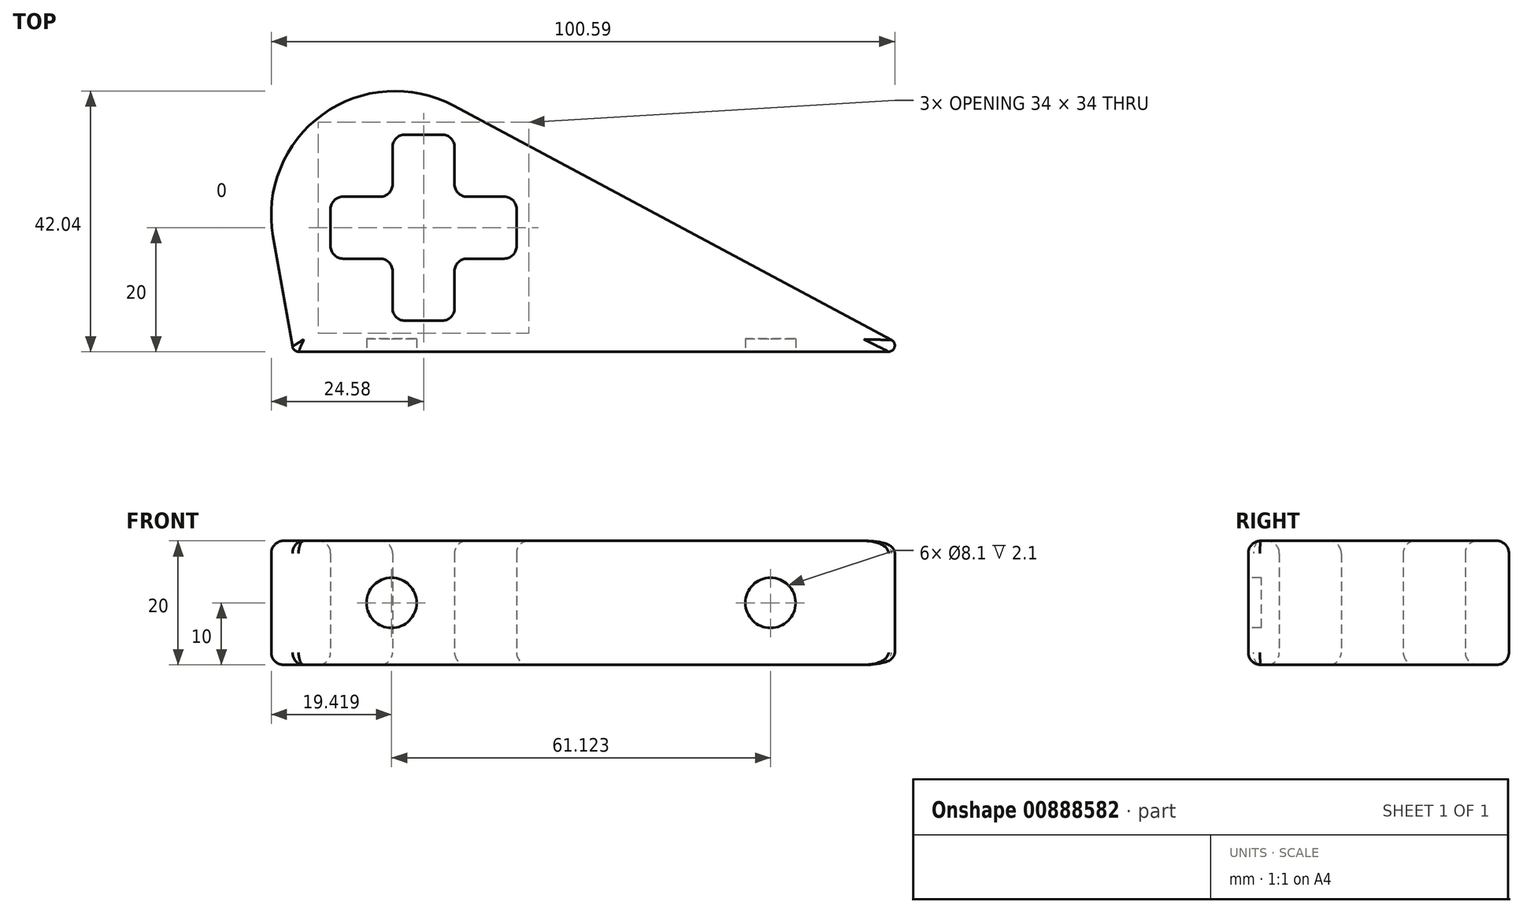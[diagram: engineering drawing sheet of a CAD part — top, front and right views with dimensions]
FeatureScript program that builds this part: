
annotation { "Feature Type Name" : "Feature", "Feature Type Description" : "" }
export const myFeature = defineFeature(function(context is Context, id is Id, definition is map)
    precondition{}
    {
        {
            var Q0;
            Q0=qCreatedBy(makeId("Top.planeOp"),FACE);
            var sketch = newSketch(context, id + "F0", { "sketchPlane" : qUnion([Q0])});
            skLineSegment(sketch, "E0.bottom", {"start": v(-13, -5) * mm, "end": v(-7, -5) * mm});
            skLineSegment(sketch, "E0.top", {"start": v(-13, 5) * mm, "end": v(-7, 5) * mm});
            skLineSegment(sketch, "E0.left", {"start": v(-15, -3) * mm, "end": v(-15, 3) * mm});
            skLineSegment(sketch, "E0.right", {"start": v(15, -3) * mm, "end": v(15, 3) * mm});
            skPoint(sketch, "E0.middle", {"position": v(0, 0) * mm});
            skPoint(sketch, "E1.visualSharp", {"position": v(-15, 5) * mm});
            skArc(sketch, "E1.filletArc", {"start": v(-13, 5) * mm, "mid": v(-14.41, 4.41) * mm, "end": v(-15, 3) * mm});
            skPoint(sketch, "E2.visualSharp", {"position": v(15, 5) * mm});
            skArc(sketch, "E2.filletArc", {"start": v(15, 3) * mm, "mid": v(14.41, 4.41) * mm, "end": v(13, 5) * mm});
            skPoint(sketch, "E3.visualSharp", {"position": v(15, -5) * mm});
            skArc(sketch, "E3.filletArc", {"start": v(13, -5) * mm, "mid": v(14.41, -4.41) * mm, "end": v(15, -3) * mm});
            skPoint(sketch, "E4.visualSharp", {"position": v(-15, -5) * mm});
            skArc(sketch, "E4.filletArc", {"start": v(-15, -3) * mm, "mid": v(-14.41, -4.41) * mm, "end": v(-13, -5) * mm});
            skLineSegment(sketch, "E5", {"start": v(-20.16, -20) * mm, "end": v(75.01, -20) * mm});
            skLineSegment(sketch, "E6", {"start": v(75.48, -18.12) * mm, "end": v(4.86, 19.68) * mm});
            skLineSegment(sketch, "E7", {"start": v(-24.27, -1.43) * mm, "end": v(-21.15, -19.17) * mm});
            skPoint(sketch, "E8.visualSharp", {"position": v(-31.42, 39.09) * mm});
            skArc(sketch, "E8.filletArc", {"start": v(4.86, 19.68) * mm, "mid": v(-16.31, 18.24) * mm, "end": v(-24.27, -1.43) * mm});
            skPoint(sketch, "E9.visualSharp", {"position": v(79, -20) * mm});
            skArc(sketch, "E9.filletArc", {"start": v(75.01, -20) * mm, "mid": v(75.98, -19.24) * mm, "end": v(75.48, -18.12) * mm});
            skPoint(sketch, "E10.visualSharp", {"position": v(-21, -20) * mm});
            skArc(sketch, "E10.filletArc", {"start": v(-21.15, -19.17) * mm, "mid": v(-20.8, -19.77) * mm, "end": v(-20.16, -20) * mm});
            skLineSegment(sketch, "E11.bottom", {"start": v(-3, -15) * mm, "end": v(3, -15) * mm});
            skLineSegment(sketch, "E11.top", {"start": v(-3, 15) * mm, "end": v(3, 15) * mm});
            skLineSegment(sketch, "E11.left", {"start": v(-5, -13) * mm, "end": v(-5, -7) * mm});
            skLineSegment(sketch, "E11.right", {"start": v(5, -13) * mm, "end": v(5, -7) * mm});
            skPoint(sketch, "E12.visualSharp", {"position": v(-5, 15) * mm});
            skArc(sketch, "E12.filletArc", {"start": v(-3, 15) * mm, "mid": v(-4.41, 14.41) * mm, "end": v(-5, 13) * mm});
            skPoint(sketch, "E13.visualSharp", {"position": v(5, 15) * mm});
            skArc(sketch, "E13.filletArc", {"start": v(5, 13) * mm, "mid": v(4.41, 14.41) * mm, "end": v(3, 15) * mm});
            skPoint(sketch, "E14.visualSharp", {"position": v(-5, -15) * mm});
            skArc(sketch, "E14.filletArc", {"start": v(-5, -13) * mm, "mid": v(-4.41, -14.41) * mm, "end": v(-3, -15) * mm});
            skPoint(sketch, "E15.visualSharp", {"position": v(5, -15) * mm});
            skArc(sketch, "E15.filletArc", {"start": v(3, -15) * mm, "mid": v(4.41, -14.41) * mm, "end": v(5, -13) * mm});
            skLineSegment(sketch, "E16.trimOffspring", {"start": v(-5, 7) * mm, "end": v(-5, 13) * mm});
            skLineSegment(sketch, "E17.trimOffspring", {"start": v(7, 5) * mm, "end": v(13, 5) * mm});
            skLineSegment(sketch, "E18.trimOffspring", {"start": v(5, 7) * mm, "end": v(5, 13) * mm});
            skLineSegment(sketch, "E19.trimOffspring", {"start": v(7, -5) * mm, "end": v(13, -5) * mm});
            skPoint(sketch, "E20.visualSharp", {"position": v(-5, 5) * mm});
            skArc(sketch, "E20.filletArc", {"start": v(-7, 5) * mm, "mid": v(-5.59, 5.59) * mm, "end": v(-5, 7) * mm});
            skPoint(sketch, "E21.visualSharp", {"position": v(5, 5) * mm});
            skArc(sketch, "E21.filletArc", {"start": v(5, 7) * mm, "mid": v(5.59, 5.59) * mm, "end": v(7, 5) * mm});
            skPoint(sketch, "E22.visualSharp", {"position": v(5, -5) * mm});
            skArc(sketch, "E22.filletArc", {"start": v(7, -5) * mm, "mid": v(5.59, -5.59) * mm, "end": v(5, -7) * mm});
            skPoint(sketch, "E23.visualSharp", {"position": v(-5, -5) * mm});
            skArc(sketch, "E23.filletArc", {"start": v(-5, -7) * mm, "mid": v(-5.59, -5.59) * mm, "end": v(-7, -5) * mm});
            skSolve(sketch);
        }
        {
            var Q0;
            Q0 = qSketchRegion(id + "F0", true);
            extrude(context, id + "F1", {"entities" : qUnion([Q0]), "depth" : 20 * mm, "offsetDistance" : 25 * mm});
        }
        {
            var Q0;
            Q0=makeQuery(id+"F1.opExtrude","CAP_FACE",FACE,{"disambiguationData":[OSD([sQuery(id+"F0.wireOp",EDGE,"E0.bottom"),sQuery(id+"F0.wireOp",EDGE,"E0.top"),sQuery(id+"F0.wireOp",EDGE,"E0.left"),sQuery(id+"F0.wireOp",EDGE,"E0.right"),sQuery(id+"F0.wireOp",EDGE,"E1.filletArc"),sQuery(id+"F0.wireOp",EDGE,"E2.filletArc"),sQuery(id+"F0.wireOp",EDGE,"E3.filletArc"),sQuery(id+"F0.wireOp",EDGE,"E4.filletArc"),sQuery(id+"F0.wireOp",EDGE,"E5"),sQuery(id+"F0.wireOp",EDGE,"E6"),sQuery(id+"F0.wireOp",EDGE,"E7"),sQuery(id+"F0.wireOp",EDGE,"E8.filletArc"),sQuery(id+"F0.wireOp",EDGE,"E9.filletArc"),sQuery(id+"F0.wireOp",EDGE,"E10.filletArc")])],"isStart":false});
            var Q1;
            Q1=makeQuery(id+"F1.opExtrude","CAP_FACE",FACE,{"disambiguationData":[OSD([sQuery(id+"F0.wireOp",EDGE,"E0.bottom"),sQuery(id+"F0.wireOp",EDGE,"E0.top"),sQuery(id+"F0.wireOp",EDGE,"E0.left"),sQuery(id+"F0.wireOp",EDGE,"E0.right"),sQuery(id+"F0.wireOp",EDGE,"E1.filletArc"),sQuery(id+"F0.wireOp",EDGE,"E2.filletArc"),sQuery(id+"F0.wireOp",EDGE,"E3.filletArc"),sQuery(id+"F0.wireOp",EDGE,"E4.filletArc"),sQuery(id+"F0.wireOp",EDGE,"E5"),sQuery(id+"F0.wireOp",EDGE,"E6"),sQuery(id+"F0.wireOp",EDGE,"E7"),sQuery(id+"F0.wireOp",EDGE,"E8.filletArc"),sQuery(id+"F0.wireOp",EDGE,"E9.filletArc"),sQuery(id+"F0.wireOp",EDGE,"E10.filletArc")])],"isStart":true});
            fillet(context, id + "F2", {"entities" : qUnion([Q0, Q1]), "radius" : 2 * mm, "tangentPropagation" : true, "allowEdgeOverflow" : false});
        }
        {
            var Q0;
            Q0=makeQuery(id+"F1.opExtrude","SWEPT_FACE",FACE,{"disambiguationData":[OSD([sQuery(id+"F0.wireOp",EDGE,"E5")])]});
            var sketch = newSketch(context, id + "F3", { "sketchPlane" : qUnion([Q0])});
            skCircle(sketch, "E24", {"center": v(-5.16, 10) * mm, "radius": 4.05 * mm});
            skCircle(sketch, "E25", {"center": v(55.96, 10) * mm, "radius": 4.05 * mm});
            skSolve(sketch);
        }
        {
            var Q0;
            Q0 = qSketchRegion(id + "F3", true);
            extrude(context, id + "F4", {"entities" : qUnion([Q0]), "operationType" : NewBodyOperationType.REMOVE, "oppositeDirection" : true, "depth" : 2.1 * mm, "offsetDistance" : 25 * mm});
        }
    });
